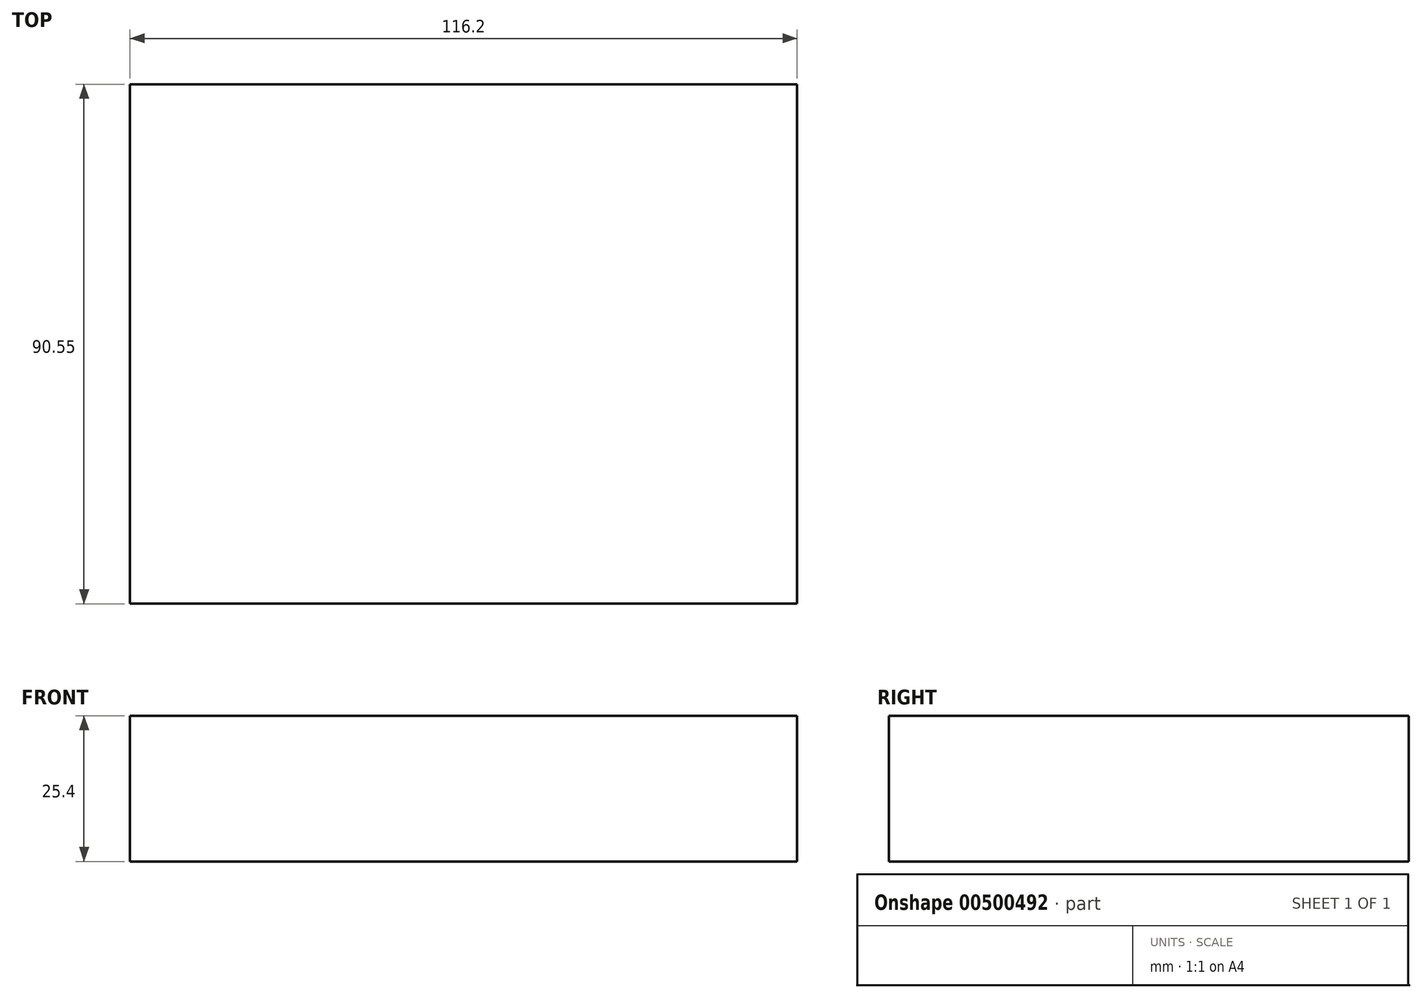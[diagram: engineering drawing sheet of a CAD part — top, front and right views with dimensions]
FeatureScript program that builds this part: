
annotation { "Feature Type Name" : "Feature", "Feature Type Description" : "" }
export const myFeature = defineFeature(function(context is Context, id is Id, definition is map)
    precondition{}
    {
        {
            var Q0;
            Q0=qCreatedBy(makeId("Top.planeOp"),FACE);
            var sketch = newSketch(context, id + "F0", { "sketchPlane" : qUnion([Q0])});
            skLineSegment(sketch, "E0.bottom", {"start": v(-54.49, 43.93) * mm, "end": v(61.7, 43.93) * mm});
            skLineSegment(sketch, "E0.top", {"start": v(-54.49, -46.62) * mm, "end": v(61.7, -46.62) * mm});
            skLineSegment(sketch, "E0.left", {"start": v(-54.49, 43.93) * mm, "end": v(-54.49, -46.62) * mm});
            skLineSegment(sketch, "E0.right", {"start": v(61.7, 43.93) * mm, "end": v(61.7, -46.62) * mm});
            skSolve(sketch);
        }
        {
            var Q0;
            Q0=makeQuery(id+"F0.imprint","IMPRINT",FACE,{"disambiguationData":[TD([[makeQuery(id+"F0.imprint","IMPRINT",EDGE,{"derivedFrom":sQuery(id+"F0.wireOp",EDGE,"E0.bottom")}),-1.0]])]});
            extrude(context, id + "F1", {"entities" : qUnion([Q0]), "depth" : 25.4 * mm});
        }
    });
